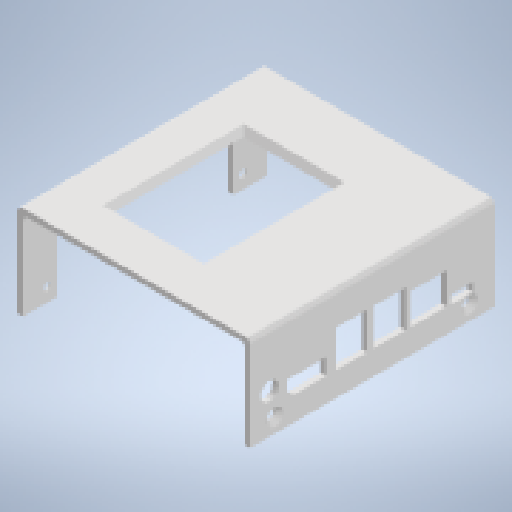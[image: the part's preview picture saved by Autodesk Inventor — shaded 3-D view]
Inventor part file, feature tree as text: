
AUTODESK INVENTOR PART (.ipt)
format: ipt  version: 2024 (Build 280153000, 153)  size: 273,920 bytes
history: native  units: mm
features: reference x12, sketch x4, extrude x4, other x4, plane x2, chamfer x2
ambient origin geometry x8: Origin, YZ Plane, XZ Plane, XY Plane, X Axis, Y Axis, Z Axis, Center Point
bodies: Solid1 (feature_tree)
feature tree (28):
  sketch  "Sketch1"  dims[d0=2.5mm d1=2.5mm]
  plane  "Work Plane1"
  extrude  "Extrusion1"  Depth=2.5mm
  extrude  "Extrusion2"  Depth=2.0mm
  chamfer  "Chamfer1"  Distance=10.0mm
  sketch  "Sketch3"  dims[d6=10.0mm d7=0.0mm d8=2.5mm d9=2.0mm d10=45.0deg]
  plane  "Work Plane2"
  extrude  "Extrusion3"  Depth=2.5mm TaperAngle=45.0deg
  extrude  "Extrusion4"  Depth=0.25mm
  chamfer  "Chamfer2"  Distance=3.5mm
  sketch  "Sketch2"  dims[d2=2.5mm d3=2.0mm d4=10.0mm d5=0.0mm]
  reference  "Reference2"
  sketch  "Sketch4"  dims[d11=10.0mm d12=0.0mm d13=3.5mm d14=3.5mm d15=8.0mm d16=3.5mm d17=3.5mm d18=0.25mm d20=0.25mm d23=0.25mm d24=0.25mm d25=0.25mm d26=0.25mm d27=0.25mm d28=0.25mm d29=0.25mm d30=0.25mm d31=0.25mm d32=0.25mm d33=0.25mm d34=0.5mm d35=0.5mm d36=0.75mm d37=0.75mm d38=10.0mm d39=0.0mm d40=2.0mm d41=2.0mm d42=45.0deg d43=40.0mm d44=39.0mm d45=0.5mm d46=0.25mm d47=0.25mm d48=0.25mm d49=0.25mm d50=0.25mm d51=0.25mm d52=0.0mm]
  reference  "Reference4"
  reference  "Reference5"
  reference  "Reference6"
  reference  "Reference7"
  reference  "Reference8"
  reference  "Reference9"
  reference  "Reference16"
  reference  "Reference17"
  reference  "Reference18"
  reference  "Reference19"
  reference  "Reference20"
  parser-record x1  (decoder bookkeeping rows leaked as tree rows — omitted from the tree; the rows remain in map.json)
  other  "REV 3 assembly.iam"
  other  "Top3518_3668_A02_3509_A01_0204:1"
  other  "TA07 ELECTRONICS MOUNT REV 3:1"
note: 1 file-system path scrubbed to <path> (originals preserved in map.json)
